# Revit family: BuzziSpace - BuzziSurf
name_source: partatom
category: Lighting Fixtures
units: mm (PartAtom-declared; Revit-internal decimal feet)

## family parameters
Always vertical = Yes
Cut with Voids When Loaded = No
Host = Ceiling
Light Source = No
Part Type = Normal
Room Calculation Point = No
Round Connector Dimension = Use Diameter
Shared = No

## types (9) — shared parameters
Black = Black
Ceiling Suspended Straight = Yes
Manufacturer = BuzziSpace
Reflector = <By Category>

## per-type parameters (varying)
| type | Canopy Width | Globe | Large Visibility | Light Spacing | Model | Quintet Light Visibility | Retrofit | Solo Visibility | Spot Light | Trio Light Visibility | Width |
| Sol Solo Spot | 12.5 cm | No | No | 37.5 cm | BuzziSurf Sol Solo Spot | No | No | Yes | Yes | No | 108 cm |
| Sol Solo Globe | 12.5 cm | Yes | No | 37.5 cm | BuzziSurf Sol Solo Globe | No | No | Yes | No | No | 108 cm |
| Sol Trio Globe | 35 cm | Yes | Yes | 40 cm | BuzziSurf Sol Trio Globe | No | No | No | No | Yes | 140 cm |
| Sol Trio Spot | 35 cm | Yes | Yes | 40 cm | BuzziSurf Sol Trio Spot | No | No | No | No | Yes | 140 cm |
| Sol Quintet Globe | 45 cm | Yes | Yes | 37.5 cm | BuzziSurf Sol Quintet Globe | Yes | No | No | No | Yes | 210 cm |
| Sol Quintet Spot | 45 cm | No | Yes | 37.5 cm | BuzziSurf Sol Quintet Spot | Yes | No | No | Yes | Yes | 210 cm |
| Sol Quintet Retrofit | 45 cm | No | Yes | 37.5 cm | BuzziSurf Sol Quintet Retrofit | Yes | Yes | No | No | Yes | 210 cm |
| Sol Solo Retrofit | 12.5 cm | No | No | 37.5 cm | BuzziSurf Sol Solo Retrofit | No | Yes | Yes | No | No | 108 cm |
| Sol Trio Retrofit | 35 cm | No | Yes | 40 cm | BuzziSurf Sol Trio Retrofit | No | Yes | No | No | Yes | 140 cm |

## geometry (parser evidence)
native form markers: Sweep x5
no freeform markers — native parametric forms only
